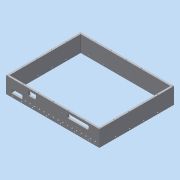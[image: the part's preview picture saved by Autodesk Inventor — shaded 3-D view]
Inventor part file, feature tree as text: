
AUTODESK INVENTOR PART (.ipt)
format: ipt  version: 2016 (Build 200138000, 138)  size: 580,608 bytes
history: native  units: in
note: dims shown in document units (in); Inventor stores cm internally (conversion verified against a paired STEP export)
features: hole x16, other x10, pattern_linear x10, fillet x8, extrude x4, projected_geometry x1, sketch x1
ambient origin geometry x8: Origin, YZ Plane, XZ Plane, XY Plane, X Axis, Y Axis, Z Axis, Center Point
bodies: Solid1 (feature_tree)
feature tree (50):
  extrude  "Extrusion1"  Depth=7.626in
  other  "left-2"
  other  "left-1"
  other  "bottom-1"
  hole  "Hole8"  [1 undecoded]
  hole  "Hole9"  [1 undecoded]
  other  "front-1"
  hole  "Hole10"  [1 undecoded]
  other  "right-1"
  hole  "Hole11"  [1 undecoded]
  hole  "Hole12"  [1 undecoded]
  pattern_linear  "Rectangular Pattern9"  Spacing1=0.0935in  [1 undecoded]
  pattern_linear  "Rectangular Pattern10"  Spacing1=0.0935in  [1 undecoded]
  pattern_linear  "Rectangular Pattern11"  Count1=6 Spacing1=1.562in
  pattern_linear  "Rectangular Pattern12"  Count1=7 Spacing1=1.635in
  hole  "Hole13"  [1 undecoded]
  hole  "Hole16"  [1 undecoded]
  hole  "Hole17"  [1 undecoded]
  extrude  "Extrusion2"  Depth=0.187in
  hole  "Hole18"  [1 undecoded]
  hole  "Hole19"  [1 undecoded]
  hole  "Hole20"  [1 undecoded]
  hole  "Hole21"  [1 undecoded]
  pattern_linear  "Rectangular Pattern13"  Spacing1=1.1693in  [1 undecoded]
  hole  "Hole22"  [1 undecoded]
  pattern_linear  "Rectangular Pattern14"  Spacing1=2.05in  [1 undecoded]
  pattern_linear  "Rectangular Pattern15"  Spacing1=0.41in  [1 undecoded]
  pattern_linear  "Rectangular Pattern16"  Spacing1=0.368in  [1 undecoded]
  pattern_linear  "Rectangular Pattern17"  Spacing1=1.0in  [1 undecoded]
  pattern_linear  "Rectangular Pattern19"  Spacing1=1.75in  [1 undecoded]
  fillet  "Fillet1"  Radius=0.185in
  fillet  "Fillet2"  Radius=1.0in
  fillet  "Fillet3"  Radius=0.185in
  fillet  "Fillet4"  Radius=0.185in
  fillet  "Fillet5"  Radius=1.75in
  fillet  "Fillet6"  Radius=0.185in
  fillet  "Fillet7"  Radius=0.3937in
  fillet  "Fillet8"  Radius=0.562in
  other  "dsub37"
  other  "dsub9"
  hole  "Hole_jackpost_dsub37"  [1 undecoded]
  extrude  "dsub37 cutout"  Depth=0.187in
  hole  "Hole_jackpost_dsub9"  [1 undecoded]
  extrude  "dsub9 cutout"  Depth=0.187in
  hole  "Hole26"  [1 undecoded]
  other  "Ext-Sketch"
  other  "back-1"
  other  "top"
  projected_geometry  "Projected Loop3"
  sketch  "Sketch30"  dims[d6=9.626in d8=7.626in d9=8.0in d10=10.0in d11=0.187in d12=0.187in d13=1.75in d14=0.0in d125=0.0935in d126=0.0935in d127=0.067in d128=0.2in d129=0.375in d130=0.25in d131=0.5635in d132=0.2in d133=0.8108in d134=2.3622in d136=1.562in d137=2.7559in d139=1.635in d140=0.0935in d141=0.0935in d142=0.067in d143=0.2in d144=0.375in d145=0.25in d146=0.5635in d147=0.2in d148=0.8108in d149=2.3622in d151=1.562in d152=2.7559in d154=1.635in d155=0.096in d156=0.75in d157=0.16in d158=0.25in d159=0.5635in d160=1.0in d161=0.8108in d162=0.096in d163=0.75in d164=0.16in d165=0.25in d166=0.5635in d167=1.0in d168=0.8108in d169=0.096in d170=0.75in d171=0.16in d172=0.25in d173=0.5635in d174=1.0in d175=0.8108in d176=0.095in d177=0.095in d180=0.067in d181=0.2in d182=0.375in d183=0.25in d184=0.5635in d185=0.2in d186=0.8108in d197=0.24in d203=0.48in d222=1.1693in d223=0.4094in d224=2.05in d225=0.41in d227=0.368in d238=0.067in d239=0.75in d240=0.375in d241=0.25in d242=0.5635in d243=1.0in d244=0.8108in d245=0.17in d246=0.75in d247=0.375in d248=0.25in d249=0.5635in d250=1.0in d251=0.8108in d252=1.0in d253=0.0in d254=1.75in d255=0.185in d256=1.0in d257=0.185in d259=0.185in d260=1.75in d261=0.185in d262=0.096in d263=0.75in d264=0.16in d265=0.25in d266=0.5635in d267=1.0in d268=0.8108in d271=6.2992in d273=0.5in d274=0.3937in d276=1.0in d278=0.17in d279=0.75in d280=0.375in d281=0.25in d282=0.5635in d283=1.0in d284=0.8108in d285=0.17in d286=0.75in d287=0.375in d288=0.25in d289=0.5635in d290=1.0in d291=0.8108in d292=0.067in d293=0.75in d294=0.375in d295=0.25in d296=0.5635in d297=0.2in d298=0.8108in d299=0.562in d300=2.05in d301=2.05in d302=0.65in d303=0.7874in d305=1.0in d306=0.25in d307=0.185in d308=0.096in d309=0.75in d310=0.16in d311=0.25in d312=0.5635in d313=1.0in d314=0.8108in d315=1.9685in d317=1.5in d318=2.3622in d320=1.6in d321=1.5748in d323=1.5in d324=1.5748in d326=1.5in d331=2.3622in d333=1.562in d334=2.7559in d336=1.635in d338=0.06in d339=0.06in d340=0.06in d341=0.06in d342=0.031in d343=0.031in d344=0.031in d345=0.031in d434=0.17in d477=2.3in d478=0.089in d479=0.089in d482=0.166in d483=0.166in d484=0.708in d485=0.583in d486=0.984in d490=0.23in d491=0.46in d492=0.166in d493=0.166in d496=0.089in d497=1.038in d498=0.089in d499=2.5in d500=0.264in d501=0.264in d502=0.264in d503=0.264in d504=1.983in d505=2.052in d506=0.132in d507=0.132in d508=0.132in d509=0.132in d510=0.21in d511=0.425in d515=0.085in d516=0.224in d517=0.375in d518=0.25in d519=0.5635in d520=0.187in d521=0.8108in d522=1.0in d523=0.0in d524=0.085in d525=0.224in d526=0.375in d527=0.25in d528=0.5635in d529=0.187in d530=0.8108in d531=1.0in d532=0.0in d537=0.085in d538=0.224in d539=0.375in d540=0.25in d541=0.5635in d542=0.187in d543=0.8108in d544=0.47in d545=0.47in d33=1.0in d34=1.0in d383=1.0in d384=1.0in]
note: 24 required parameter values undecoded (feature->parameter linkage not recoverable at this tier; creation-order binding heuristic only, values carry confidence <= 0.55)
